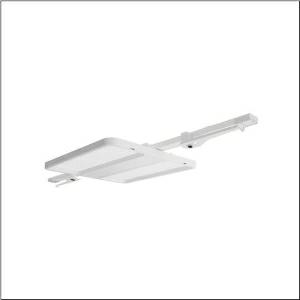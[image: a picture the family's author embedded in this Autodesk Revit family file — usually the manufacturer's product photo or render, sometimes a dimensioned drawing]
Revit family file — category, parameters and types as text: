
# Revit family: highbay_11_fur_modario_r__tragschiene_midi_51hn11da4mma_5e94
name_source: partatom
category: Lighting Fixtures
units: mm (PartAtom-declared; Revit-internal decimal feet)

## family parameters
Cut with Voids When Loaded = No
Host = Face
Light Source = No
Part Type = Normal
Room Calculation Point = No
Round Connector Dimension = Use Diameter
Shared = No

## types (1)
- --- (1 x LED, 28000 lm, 146.6 W, 4000K)
    Apparent Load = 147 VA
    CIE Flux Codes = 85 97 100 100 100
    Color Rendering = 80
    Color Temperature = 4000K
    Default Elevation = 1800 mm
    Description = high bay luminaire Highbay 11 for Modario® trunking rail midi; direct symmetric narrow distribution, light control with lens of PMMA; UGR ≤ 22 (X = 4H | Y = 8H | S = 0.25H | reflection values 70/50/20); luminous flux: 28.000lm; light colour: 840, colour temperature: 4000K, MacAdam ≤ 2 SDCM (initial), colour rendering: CRI > 80; luminous efficacy: 191lm/W; rated service life: 100.000h (L95/B50) at AT= 25°C; control: DALI 2; luminaire connection: plug, 5-pole, with phase selectionmains connection: 230..240V, AC 50/60Hz; connected load: 146,6W; protection rating (complete): IP64; insulation class (complete): insulation class I (protective earthing); protection symbol: D; impact resistance: IK07; certification: CE, ENEC, VDE, UKCA; internal wiring halogen-free; luminaire corresponds to IFS (International Featured Standards) requirements for safety and quality in the food industry; LABS conformity tested according to VDMA 24364:2018-05; housing frame of high-performance plastic PA6, matt traffic white (RAL 9016); cover of PMMA; fixing on rail side of steel, galvanised, white; blank cover of PC, traffic white (RAL 9016); dimension (LxWxH): 1.195 x 442 x 72mm; permissible operating ambient temperature: -40..+50°C (reducing of maximum allowable ambient temperature of 5°C with ceiling mounting); packaging unit: 1 piece
    Height = 72 mm  [stored 0.23622 ft]
    Lamp = 1 x LED
    Lamp Light Flux = 28000 lm
    Lamp Power = 146.6 W
    Lamp count = 1
    Length = 474 mm
    Luminous efficacy = 191 lm/W
    Manufacturer = Siteco
    ModVariant = No
    Model = 51HN11DA4MMA
    Mounting Place = Ceiling
    Mounting Type = Pendant
    Number of Poles = 1
    OnlyDefault = Yes
    Power Factor = 1
    Product Name = Highbay 11 für Modario® Tragschiene midi
    Product group = high bay luminaire
    ProductGroupID = 901
    Protection Class = Protection class I
    Protection Degree = IP 64
    RLX_Detail_Level = 1
    RLX_Emergency_Light_Flux = 0 lm
    RLX_Emergency_Type = 0
    RLX_Emergency_Type_DB = No
    RlxData = <blob elided: 18205 chars, md5=860d2174>
    Socket = socket
    Standby Power = 0 W
    System Light Flux = 28001 lm
    System Power = 147 W
    Type Comments = factory setting: luminous flux: 100 % | dim-lin: 254 | 661 mA
    Type Image = l_1363266.jpg
    URL = http://relux.com
    VarID = @adj_023133
    Voltage = 0 V
    Weight = 0.00 kg
    Width = 442 mm

note: [stored X ft] marks values corroborated as IEEE doubles in the binary element streams (Revit-internal decimal feet)

## geometry (parser evidence)
native form markers: Blend x4, Sweep x11
no freeform markers — native parametric forms only
